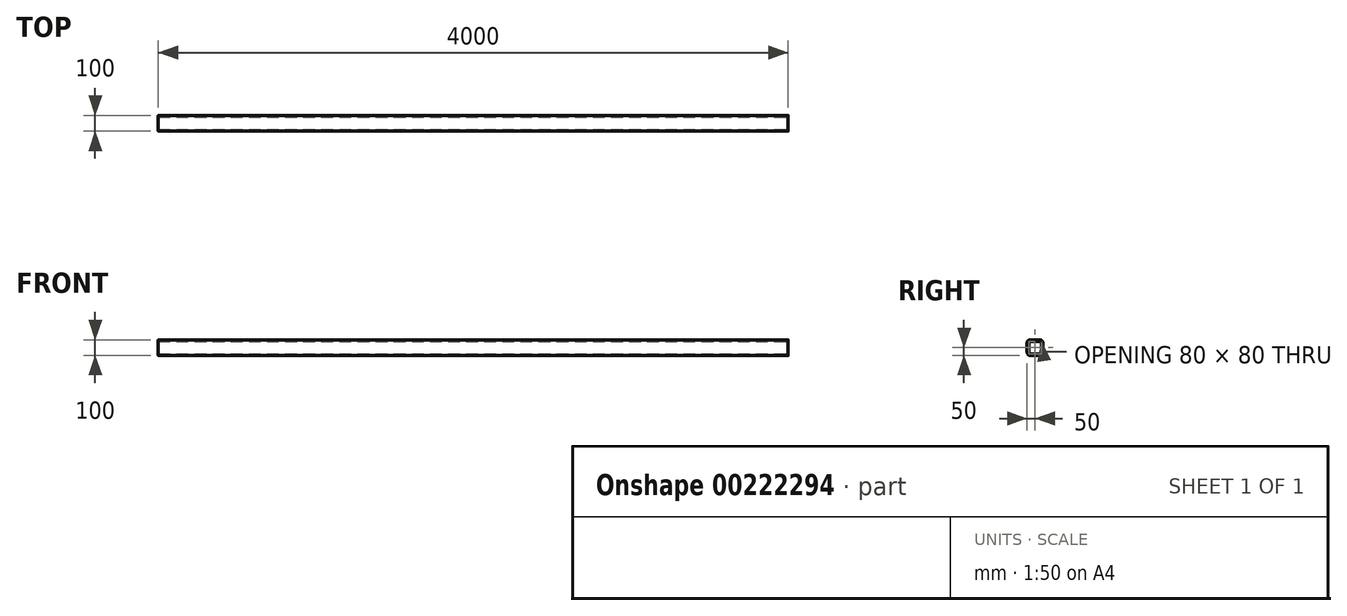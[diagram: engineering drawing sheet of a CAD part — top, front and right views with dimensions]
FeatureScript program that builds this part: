
annotation { "Feature Type Name" : "Feature", "Feature Type Description" : "" }
export const myFeature = defineFeature(function(context is Context, id is Id, definition is map)
    precondition{}
    {
        {
            var Q0;
            Q0=qCreatedBy(makeId("Top.planeOp"),FACE);
            var sketch = newSketch(context, id + "F0", { "sketchPlane" : qUnion([Q0])});
            skLineSegment(sketch, "E0.bottom", {"start": v(2000, 50) * mm, "end": v(-2000, 50) * mm});
            skLineSegment(sketch, "E0.top", {"start": v(2000, -50) * mm, "end": v(-2000, -50) * mm});
            skLineSegment(sketch, "E0.left", {"start": v(2000, 50) * mm, "end": v(2000, -50) * mm});
            skLineSegment(sketch, "E0.right", {"start": v(-2000, 50) * mm, "end": v(-2000, -50) * mm});
            skPoint(sketch, "E0.middle", {"position": v(0, 0) * mm});
            skSolve(sketch);
        }
        {
            var Q0;
            Q0=qSketchRegion(id+"F0",true);
            extrude(context, id + "F1", {"entities" : qUnion([Q0]), "depth" : 100 * mm, "offsetDistance" : 25 * mm, "symmetric" : true});
        }
        {
            var Q0;
            Q0=makeQuery(id+"F1.opExtrude","CAP_EDGE",EDGE,{"disambiguationData":[OSD([sQuery(id+"F0.wireOp",EDGE,"E0.bottom")])],"isStart":false});
            var Q1;
            Q1=makeQuery(id+"F1.opExtrude","CAP_EDGE",EDGE,{"disambiguationData":[OSD([sQuery(id+"F0.wireOp",EDGE,"E0.top")])],"isStart":true});
            var Q2;
            Q2=makeQuery(id+"F1.opExtrude","CAP_EDGE",EDGE,{"disambiguationData":[OSD([sQuery(id+"F0.wireOp",EDGE,"E0.top")])],"isStart":false});
            var Q3;
            Q3=makeQuery(id+"F1.opExtrude","CAP_EDGE",EDGE,{"disambiguationData":[OSD([sQuery(id+"F0.wireOp",EDGE,"E0.bottom")])],"isStart":true});
            fillet(context, id + "F2", {"entities" : qUnion([Q0, Q1, Q2, Q3]), "radius" : 20 * mm, "tangentPropagation" : true, "allowEdgeOverflow" : false});
        }
        {
            var Q0;
            Q0=makeQuery(id+"F1.opExtrude","SWEPT_FACE",FACE,{"disambiguationData":[OSD([sQuery(id+"F0.wireOp",EDGE,"E0.left")])]});
            var Q1;
            Q1=makeQuery(id+"F1.opExtrude","SWEPT_FACE",FACE,{"disambiguationData":[OSD([sQuery(id+"F0.wireOp",EDGE,"E0.right")])]});
            shell(context, id + "F3", {"entities" : qUnion([Q0, Q1]), "thickness" : 10 * mm});
        }
        {
            var Q0;
            Q0=makeQuery(id+"F1.opExtrude","SWEPT_BODY",BODY,{"disambiguationData":[OSD([sQuery(id+"F0.wireOp",EDGE,"E0.bottom"),sQuery(id+"F0.wireOp",EDGE,"E0.top"),sQuery(id+"F0.wireOp",EDGE,"E0.left"),sQuery(id+"F0.wireOp",EDGE,"E0.right")])]});
            var Q1;
            Q1=qCreatedBy(makeId("Right.planeOp"),FACE);
            mirror(context, id + "F4", {"operationType" : NewBodyOperationType.ADD, "entities" : qUnion([Q0]), "mirrorPlane" : qUnion([Q1])});
        }
    });
